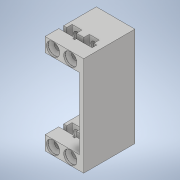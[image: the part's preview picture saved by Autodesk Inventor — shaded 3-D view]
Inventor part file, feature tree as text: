
AUTODESK INVENTOR PART (.ipt)
format: ipt  version: 2020 (Build 240168000, 168)  size: 192,512 bytes
history: native  units: mm
features: other x3, extrude x2, sketch x2, pattern_linear x1
ambient origin geometry x8: Origin, YZ Plane, XZ Plane, XY Plane, X Axis, Y Axis, Z Axis, Center Point
bodies: Solide1 (feature_tree)
feature tree (8):
  other  "base2.ipt"
  pattern_linear  "Réseau rectangulaire1"  Spacing1=10.0mm  [1 undecoded]
  extrude  "Extrusion1"  Depth=20.0mm
  extrude  "Extrusion2"  Depth=49.78mm
  other  "Solide1::base2.ipt"
  other  "FonctionRepérage1"
  sketch  "Esquisse2"
  sketch  "Esquisse3"
note: 1 required parameter value undecoded (feature->parameter linkage not recoverable at this tier; creation-order binding heuristic only, values carry confidence <= 0.55)
